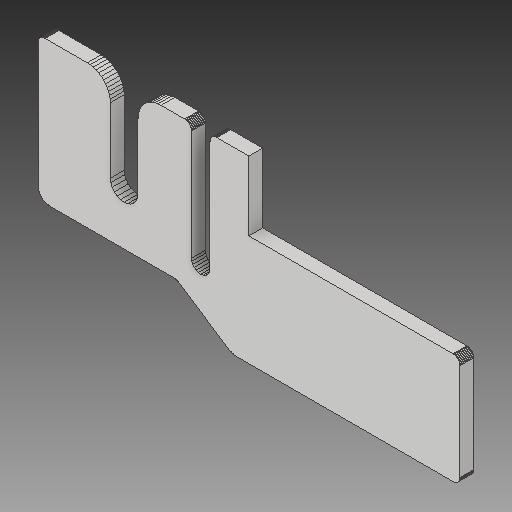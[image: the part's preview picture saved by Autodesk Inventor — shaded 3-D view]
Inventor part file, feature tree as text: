
AUTODESK INVENTOR PART (.ipt)
format: ipt  version: 2018 (Build 220112000, 112)  size: 320,512 bytes
history: native  units: mm
features: extrude x1, sketch x1
ambient origin geometry x8: Origin, YZ Plane, XZ Plane, XY Plane, X Axis, Y Axis, Z Axis, Center Point
bodies: Solid1 (feature_tree)
feature tree (2):
  extrude  "Extrusion1"  [1 undecoded]
  sketch  "Sketch1"  dims[d0=6.0mm d1=0.0mm]
note: 1 required parameter value undecoded (feature->parameter linkage not recoverable at this tier; creation-order binding heuristic only, values carry confidence <= 0.55)
